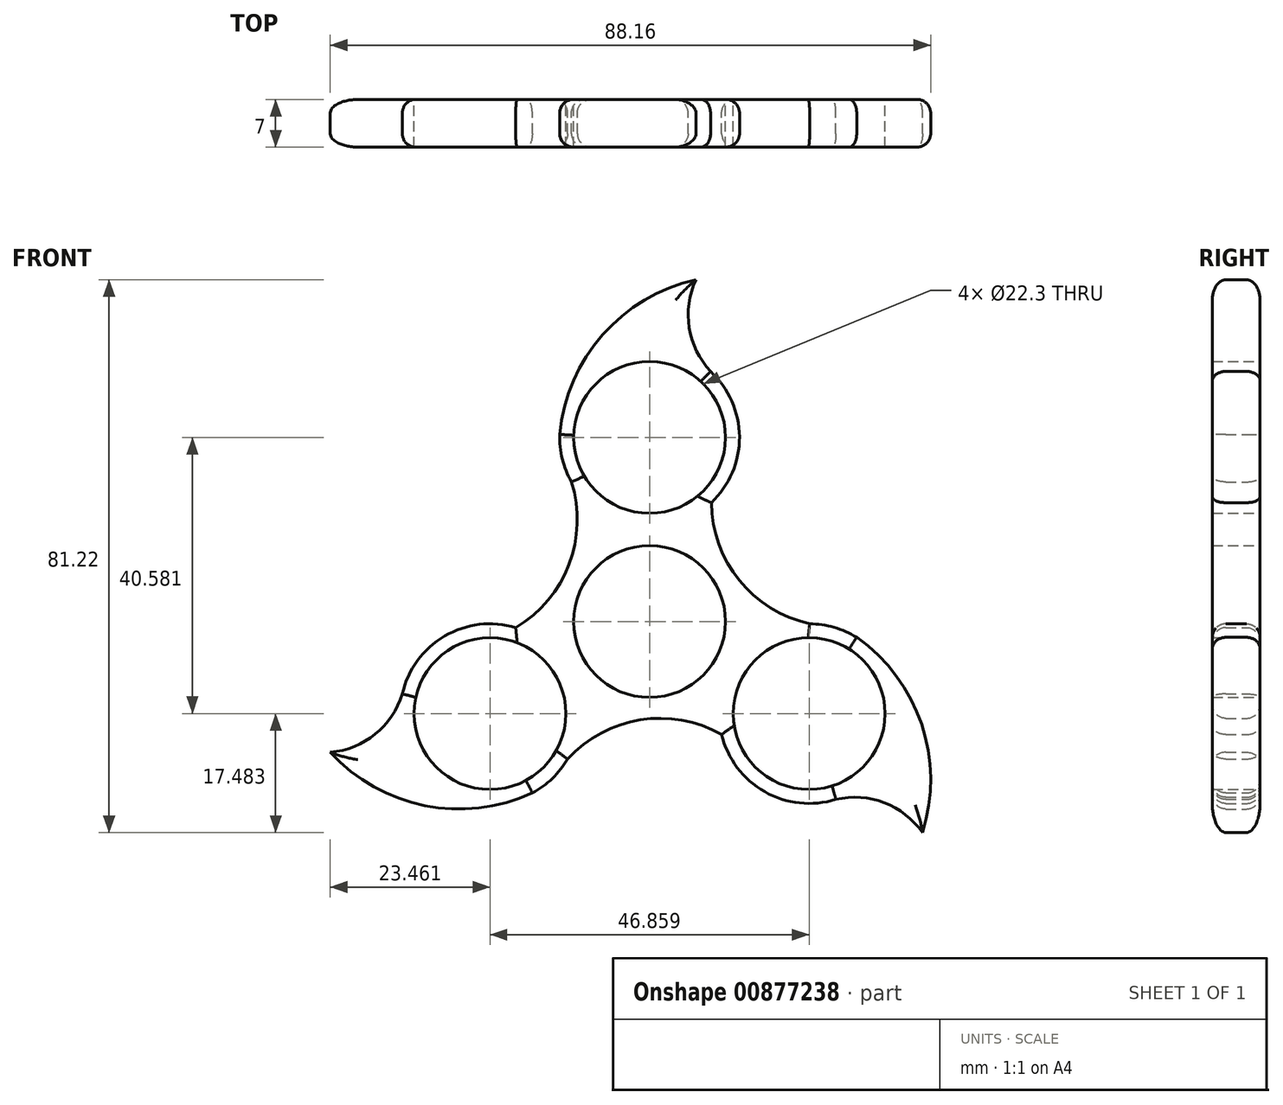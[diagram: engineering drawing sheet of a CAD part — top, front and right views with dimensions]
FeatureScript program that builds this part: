
annotation { "Feature Type Name" : "Feature", "Feature Type Description" : "" }
export const myFeature = defineFeature(function(context is Context, id is Id, definition is map)
    precondition{}
    {
        {
            var Q0;
            Q0=qCreatedBy(makeId("Front.planeOp"),FACE);
            var sketch = newSketch(context, id + "F0", { "sketchPlane" : qUnion([Q0])});
            skCircle(sketch, "E0", {"center": v(0, 0) * mm, "radius": 11.15 * mm});
            skCircle(sketch, "E1", {"center": v(0, 27.05) * mm, "radius": 11.15 * mm});
            skArc(sketch, "E2", {"start": v(9.07, 17.46) * mm, "mid": v(13.2, 27.13) * mm, "end": v(8.95, 36.75) * mm});
            skArc(sketch, "E3.1.0", {"start": v(-19.66, -0.88) * mm, "mid": v(-30.1, -2.14) * mm, "end": v(-36.3, -10.62) * mm});
            skCircle(sketch, "E3.1.1", {"center": v(-23.43, -13.53) * mm, "radius": 11.15 * mm});
            skArc(sketch, "E3.2.0", {"start": v(10.59, -16.59) * mm, "mid": v(16.9, -25) * mm, "end": v(27.35, -26.13) * mm});
            skCircle(sketch, "E3.2.1", {"center": v(23.43, -13.53) * mm, "radius": 11.15 * mm});
            skArc(sketch, "E4", {"start": v(6.81, 50.21) * mm, "mid": v(-6.9, 42.12) * mm, "end": v(-13.2, 27.5) * mm});
            skArc(sketch, "E5", {"start": v(6.81, 50.21) * mm, "mid": v(5.82, 43.16) * mm, "end": v(8.95, 36.75) * mm});
            skArc(sketch, "E6.1.0", {"start": v(-46.9, -19.2) * mm, "mid": v(-33.03, -27.04) * mm, "end": v(-17.22, -25.17) * mm});
            skArc(sketch, "E6.1.1", {"start": v(-46.9, -19.2) * mm, "mid": v(-40.28, -16.54) * mm, "end": v(-36.3, -10.62) * mm});
            skArc(sketch, "E6.2.0", {"start": v(40.08, -31) * mm, "mid": v(39.93, -15.08) * mm, "end": v(30.4, -2.32) * mm});
            skArc(sketch, "E6.2.1", {"start": v(40.08, -31) * mm, "mid": v(34.46, -26.62) * mm, "end": v(27.35, -26.13) * mm});
            skArc(sketch, "E7", {"start": v(-19.66, -0.88) * mm, "mid": v(-11.84, 8.4) * mm, "end": v(-11.47, 20.52) * mm});
            skArc(sketch, "E8.1.0", {"start": v(10.59, -16.59) * mm, "mid": v(-1.35, -14.45) * mm, "end": v(-12.03, -20.19) * mm});
            skArc(sketch, "E8.2.0", {"start": v(9.07, 17.46) * mm, "mid": v(13.19, 6.05) * mm, "end": v(23.5, -0.33) * mm});
            skArc(sketch, "E9.trimOffspring", {"start": v(-13.2, 27.5) * mm, "mid": v(-12.81, 23.89) * mm, "end": v(-11.47, 20.52) * mm});
            skPoint(sketch, "E10.orphan", {"position": v(9.61, 36.1) * mm});
            skArc(sketch, "E11.trimOffspring", {"start": v(30.4, -2.32) * mm, "mid": v(27.1, -0.85) * mm, "end": v(23.5, -0.33) * mm});
            skArc(sketch, "E12.trimOffspring", {"start": v(-17.22, -25.17) * mm, "mid": v(-14.28, -23.04) * mm, "end": v(-12.03, -20.19) * mm});
            skPoint(sketch, "E13.orphan", {"position": v(-36.07, -9.73) * mm});
            skPoint(sketch, "E14.orphan", {"position": v(26.46, -26.37) * mm});
            skSolve(sketch);
        }
        {
            var Q0;
            Q0 = qSketchRegion(id + "F0", true);
            extrude(context, id + "F1", {"entities" : qUnion([Q0]), "depth" : 7 * mm, "offsetDistance" : 25 * mm});
        }
        {
            var Q0;
            Q0=makeQuery(id+"F1.opExtrude","CAP_EDGE",EDGE,{"disambiguationData":[OSD([sQuery(id+"F0.wireOp",EDGE,"E7")])],"isStart":true});
            var Q1;
            Q1=makeQuery(id+"F1.opExtrude","CAP_EDGE",EDGE,{"disambiguationData":[OSD([sQuery(id+"F0.wireOp",EDGE,"E9.trimOffspring")])],"isStart":true});
            var Q2;
            Q2=makeQuery(id+"F1.opExtrude","CAP_EDGE",EDGE,{"disambiguationData":[OSD([sQuery(id+"F0.wireOp",EDGE,"E4")])],"isStart":true});
            var Q3;
            Q3=makeQuery(id+"F1.opExtrude","CAP_EDGE",EDGE,{"disambiguationData":[OSD([sQuery(id+"F0.wireOp",EDGE,"E3.1.0")])],"isStart":true});
            var Q4;
            Q4=makeQuery(id+"F1.opExtrude","CAP_EDGE",EDGE,{"disambiguationData":[OSD([sQuery(id+"F0.wireOp",EDGE,"E5")])],"isStart":true});
            var Q5;
            Q5=makeQuery(id+"F1.opExtrude","CAP_EDGE",EDGE,{"disambiguationData":[OSD([sQuery(id+"F0.wireOp",EDGE,"E2")])],"isStart":true});
            var Q6;
            Q6=makeQuery(id+"F1.opExtrude","CAP_EDGE",EDGE,{"disambiguationData":[OSD([sQuery(id+"F0.wireOp",EDGE,"E8.2.0")])],"isStart":true});
            var Q7;
            Q7=makeQuery(id+"F1.opExtrude","CAP_EDGE",EDGE,{"disambiguationData":[OSD([sQuery(id+"F0.wireOp",EDGE,"E11.trimOffspring")])],"isStart":true});
            var Q8;
            Q8=makeQuery(id+"F1.opExtrude","CAP_EDGE",EDGE,{"disambiguationData":[OSD([sQuery(id+"F0.wireOp",EDGE,"E6.2.0")])],"isStart":true});
            var Q9;
            Q9=makeQuery(id+"F1.opExtrude","CAP_EDGE",EDGE,{"disambiguationData":[OSD([sQuery(id+"F0.wireOp",EDGE,"E6.2.1")])],"isStart":true});
            var Q10;
            Q10=makeQuery(id+"F1.opExtrude","CAP_EDGE",EDGE,{"disambiguationData":[OSD([sQuery(id+"F0.wireOp",EDGE,"E8.1.0")])],"isStart":true});
            var Q11;
            Q11=makeQuery(id+"F1.opExtrude","CAP_EDGE",EDGE,{"disambiguationData":[OSD([sQuery(id+"F0.wireOp",EDGE,"E3.2.0")])],"isStart":true});
            var Q12;
            Q12=makeQuery(id+"F1.opExtrude","CAP_EDGE",EDGE,{"disambiguationData":[OSD([sQuery(id+"F0.wireOp",EDGE,"E12.trimOffspring")])],"isStart":true});
            var Q13;
            Q13=makeQuery(id+"F1.opExtrude","CAP_EDGE",EDGE,{"disambiguationData":[OSD([sQuery(id+"F0.wireOp",EDGE,"E6.1.0")])],"isStart":true});
            var Q14;
            Q14=makeQuery(id+"F1.opExtrude","CAP_EDGE",EDGE,{"disambiguationData":[OSD([sQuery(id+"F0.wireOp",EDGE,"E6.1.1")])],"isStart":true});
            fillet(context, id + "F2", {"entities" : qUnion([Q0, Q1, Q2, Q3, Q4, Q5, Q6, Q7, Q8, Q9, Q10, Q11, Q12, Q13, Q14]), "radius" : 2 * mm, "tangentPropagation" : true, "allowEdgeOverflow" : false});
        }
        {
            var Q0;
            Q0=makeQuery(id+"F1.opExtrude","CAP_EDGE",EDGE,{"disambiguationData":[OSD([sQuery(id+"F0.wireOp",EDGE,"E4")])],"isStart":false});
            var Q1;
            Q1=makeQuery(id+"F1.opExtrude","CAP_EDGE",EDGE,{"disambiguationData":[OSD([sQuery(id+"F0.wireOp",EDGE,"E9.trimOffspring")])],"isStart":false});
            var Q2;
            Q2=makeQuery(id+"F1.opExtrude","CAP_EDGE",EDGE,{"disambiguationData":[OSD([sQuery(id+"F0.wireOp",EDGE,"E7")])],"isStart":false});
            var Q3;
            Q3=makeQuery(id+"F1.opExtrude","CAP_EDGE",EDGE,{"disambiguationData":[OSD([sQuery(id+"F0.wireOp",EDGE,"E3.1.0")])],"isStart":false});
            var Q4;
            Q4=makeQuery(id+"F1.opExtrude","CAP_EDGE",EDGE,{"disambiguationData":[OSD([sQuery(id+"F0.wireOp",EDGE,"E6.1.1")])],"isStart":false});
            var Q5;
            Q5=makeQuery(id+"F1.opExtrude","CAP_EDGE",EDGE,{"disambiguationData":[OSD([sQuery(id+"F0.wireOp",EDGE,"E6.1.0")])],"isStart":false});
            var Q6;
            Q6=makeQuery(id+"F1.opExtrude","CAP_EDGE",EDGE,{"disambiguationData":[OSD([sQuery(id+"F0.wireOp",EDGE,"E12.trimOffspring")])],"isStart":false});
            var Q7;
            Q7=makeQuery(id+"F1.opExtrude","CAP_EDGE",EDGE,{"disambiguationData":[OSD([sQuery(id+"F0.wireOp",EDGE,"E8.1.0")])],"isStart":false});
            var Q8;
            Q8=makeQuery(id+"F1.opExtrude","CAP_EDGE",EDGE,{"disambiguationData":[OSD([sQuery(id+"F0.wireOp",EDGE,"E3.2.0")])],"isStart":false});
            var Q9;
            {var subQ0=sQuery(id+"F0.wireOp",EDGE,"E6.2.1");Q9=makeQuery(id+"F2.opFillet","BLEND_EDGE",EDGE,{"blendedFrom":[makeQuery(id+"F1.opExtrude","CAP_EDGE",EDGE,{"disambiguationData":[OSD([subQ0])],"isStart":true}),makeQuery(id+"F1.opExtrude","SWEPT_FACE",FACE,{"disambiguationData":[OSD([subQ0])]})],"blendedInto":[makeQuery(id+"F1.opExtrude","SWEPT_FACE",FACE,{"disambiguationData":[OSD([subQ0])]})]});}
            var Q10;
            Q10=makeQuery(id+"F1.opExtrude","CAP_EDGE",EDGE,{"disambiguationData":[OSD([sQuery(id+"F0.wireOp",EDGE,"E6.2.0")])],"isStart":false});
            var Q11;
            Q11=makeQuery(id+"F1.opExtrude","CAP_EDGE",EDGE,{"disambiguationData":[OSD([sQuery(id+"F0.wireOp",EDGE,"E8.2.0")])],"isStart":false});
            var Q12;
            Q12=makeQuery(id+"F1.opExtrude","CAP_EDGE",EDGE,{"disambiguationData":[OSD([sQuery(id+"F0.wireOp",EDGE,"E11.trimOffspring")])],"isStart":false});
            var Q13;
            Q13=makeQuery(id+"F1.opExtrude","CAP_EDGE",EDGE,{"disambiguationData":[OSD([sQuery(id+"F0.wireOp",EDGE,"E2")])],"isStart":false});
            var Q14;
            Q14=makeQuery(id+"F1.opExtrude","CAP_EDGE",EDGE,{"disambiguationData":[OSD([sQuery(id+"F0.wireOp",EDGE,"E5")])],"isStart":false});
            fillet(context, id + "F3", {"entities" : qUnion([Q0, Q1, Q2, Q3, Q4, Q5, Q6, Q7, Q8, Q9, Q10, Q11, Q12, Q13, Q14]), "radius" : 2 * mm, "tangentPropagation" : true, "allowEdgeOverflow" : false});
        }
    });
